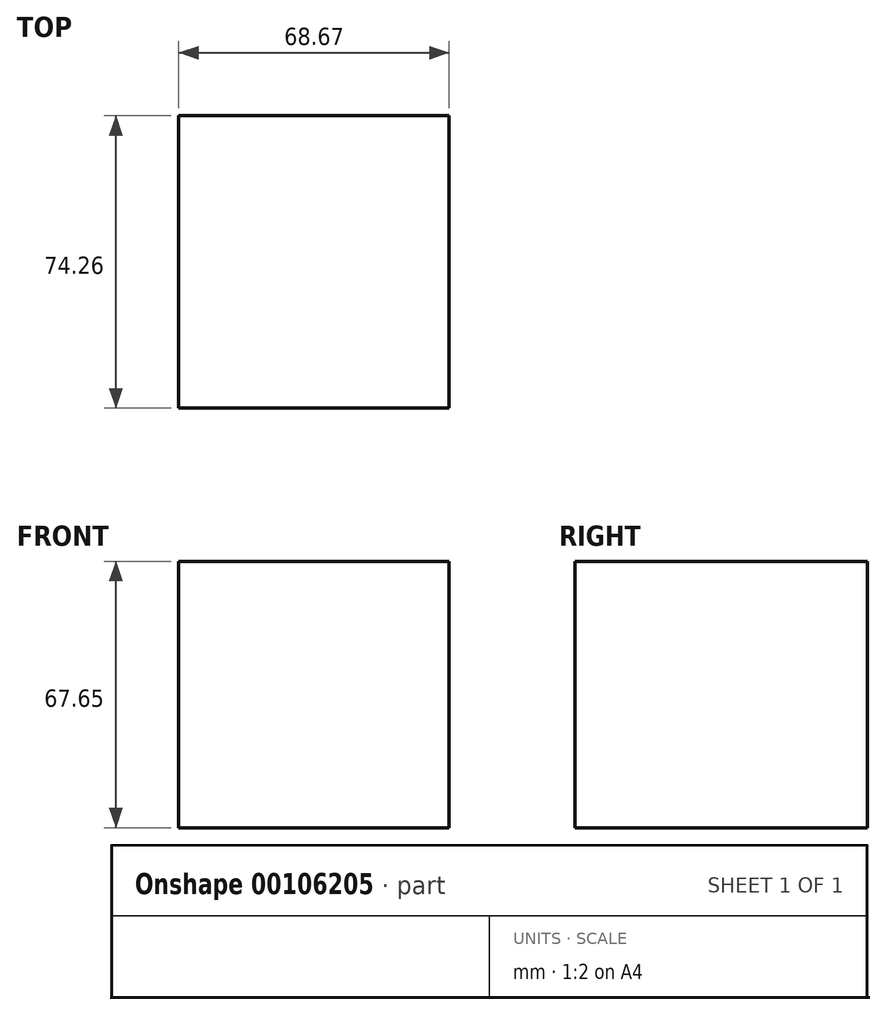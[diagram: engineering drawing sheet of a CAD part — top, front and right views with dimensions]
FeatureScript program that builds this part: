
annotation { "Feature Type Name" : "Feature", "Feature Type Description" : "" }
export const myFeature = defineFeature(function(context is Context, id is Id, definition is map)
    precondition{}
    {
        {
            var Q0;
            Q0=qCreatedBy(makeId("Front.planeOp"),FACE);
            var sketch = newSketch(context, id + "F0", { "sketchPlane" : qUnion([Q0])});
            skLineSegment(sketch, "E0.bottom", {"start": v(0, 0) * mm, "end": v(68.67, 0) * mm});
            skLineSegment(sketch, "E0.top", {"start": v(0, 67.65) * mm, "end": v(68.67, 67.65) * mm});
            skLineSegment(sketch, "E0.left", {"start": v(0, 0) * mm, "end": v(0, 67.65) * mm});
            skLineSegment(sketch, "E0.right", {"start": v(68.67, 0) * mm, "end": v(68.67, 67.65) * mm});
            skSolve(sketch);
        }
        {
            var Q0;
            Q0 = qSketchRegion(id + "F0", true);
            extrude(context, id + "F1", {"entities" : qUnion([Q0]), "depth" : 74.26 * mm});
        }
    });
